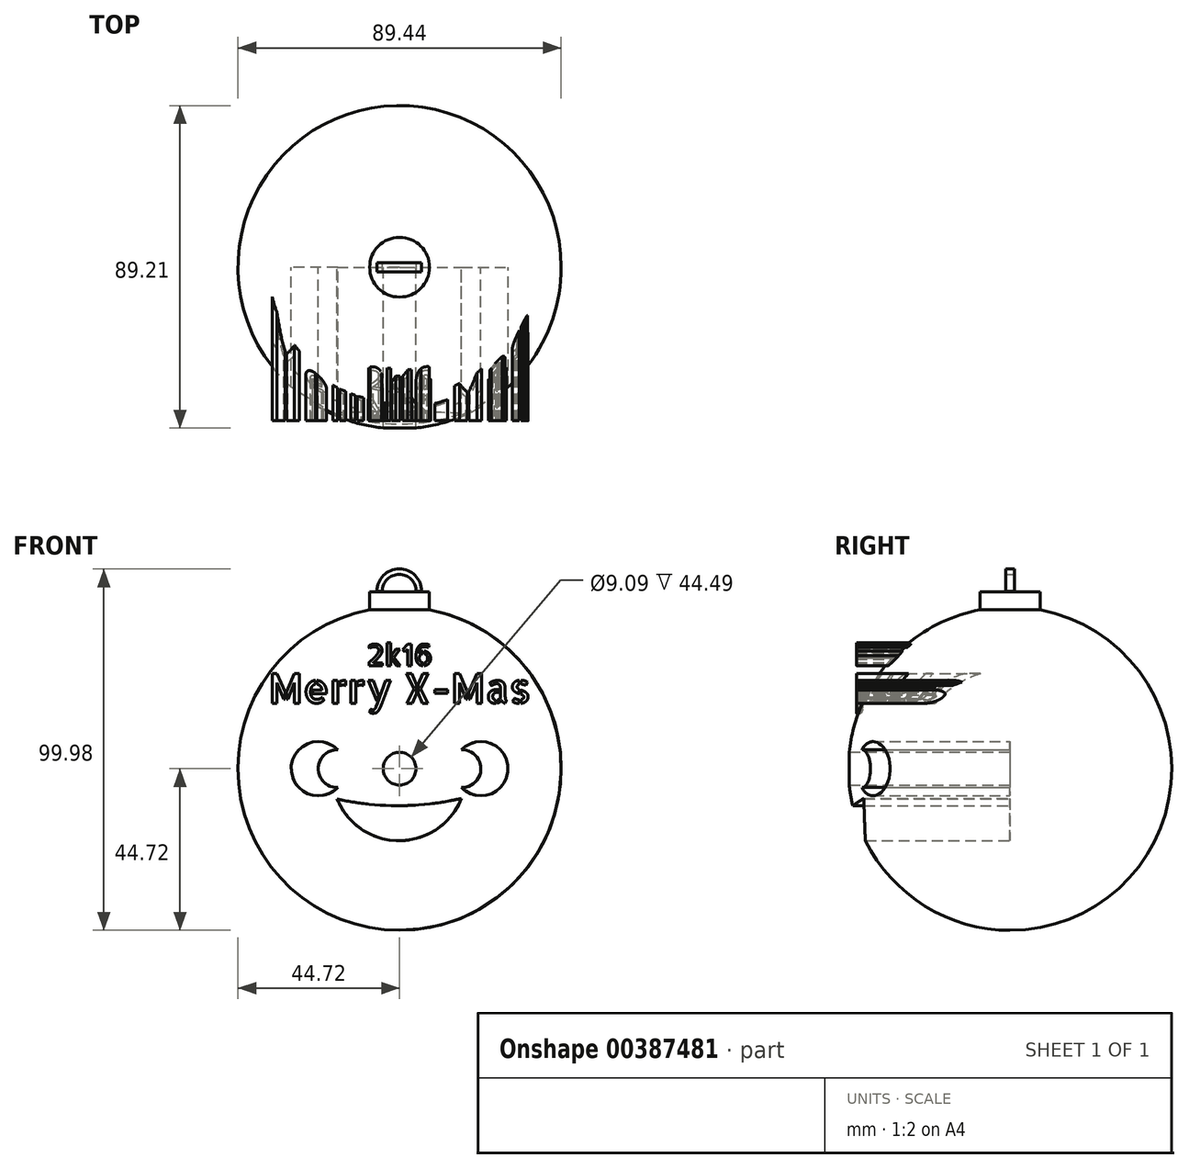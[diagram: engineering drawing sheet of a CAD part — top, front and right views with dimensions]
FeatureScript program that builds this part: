
annotation { "Feature Type Name" : "Feature", "Feature Type Description" : "" }
export const myFeature = defineFeature(function(context is Context, id is Id, definition is map)
    precondition{}
    {
        {
            var Q0;
            Q0=qCreatedBy(makeId("Front.planeOp"),FACE);
            var sketch = newSketch(context, id + "F0", { "sketchPlane" : qUnion([Q0])});
            skCircle(sketch, "E0", {"center": v(0, 0) * mm, "radius": 44.72 * mm});
            skLineSegment(sketch, "E1", {"start": v(0, 44.72) * mm, "end": v(0, -44.72) * mm});
            skSolve(sketch);
        }
        {
            var Q0;
            Q0=qCreatedBy(makeId("Front.planeOp"),FACE);
            var sketch = newSketch(context, id + "F1", { "sketchPlane" : qUnion([Q0])});
            skCircle(sketch, "E2", {"center": v(-22.5, 0) * mm, "radius": 7.5 * mm});
            skCircle(sketch, "E3", {"center": v(22.5, 0) * mm, "radius": 7.5 * mm});
            skArc(sketch, "E4", {"start": v(-17.12, 5.22) * mm, "mid": v(-22.5, 0) * mm, "end": v(-17.12, -5.22) * mm});
            skArc(sketch, "E5", {"start": v(17.12, -5.22) * mm, "mid": v(22.5, 0) * mm, "end": v(17.12, 5.22) * mm});
            skArc(sketch, "E6", {"start": v(-17.28, -8.4) * mm, "mid": v(-0.07, -10.25) * mm, "end": v(17.12, -8.21) * mm});
            skArc(sketch, "E7", {"start": v(-17.28, -8.4) * mm, "mid": v(-0.02, -19.93) * mm, "end": v(17.12, -8.21) * mm});
            skCircle(sketch, "E8", {"center": v(0, 0) * mm, "radius": 4.55 * mm});
            skSolve(sketch);
        }
        {
            var Q0;
            Q0=qCreatedBy(makeId("Front.planeOp"),FACE);
            var sketch = newSketch(context, id + "F2", { "sketchPlane" : qUnion([Q0])});
            skText(sketch, "E9", { "text": "Merry X-Mas", "fontName": "AllertaStencil-Regular.ttf"});
            skText(sketch, "E10", { "text": "2k16", "fontName": "AllertaStencil-Regular.ttf"});
            const initialGuessF2  = {"E9": [-0.03627, 0.01812, 1, 0, 0.00816], "E10": [-0.00913, 0.02852, 1, 0, 0.00594]};
            skSetInitialGuess(sketch, initialGuessF2);
            skSolve(sketch);
        }
        {
            var Q0;
            {var subQ0=sQuery(id+"F0.wireOp",EDGE,"E1");Q0=makeQuery(id+"F0.imprint","IMPRINT",FACE,{"disambiguationData":[TD([[makeQuery(id+"F0.imprint","IMPRINT",EDGE,{"derivedFrom":subQ0}),-1.0]])]});}
            var Q1;
            Q1=sQuery(id+"F0.wireOp",EDGE,"E1");
            revolve(context, id + "F3", {"entities" : qUnion([Q0]), "axis" : qUnion([Q1]), "revolveType" : RevolveType.FULL});
        }
        {
            var Q0;
            {var subQ0=sQuery(id+"F1.wireOp",EDGE,"E4");Q0=makeQuery(id+"F1.imprint","IMPRINT",FACE,{"disambiguationData":[TD([[makeQuery(id+"F1.imprint","IMPRINT",EDGE,{"derivedFrom":subQ0}),-1.0]])]});}
            var Q1;
            {var subQ0=sQuery(id+"F1.wireOp",EDGE,"E5");Q1=makeQuery(id+"F1.imprint","IMPRINT",FACE,{"disambiguationData":[TD([[makeQuery(id+"F1.imprint","IMPRINT",EDGE,{"derivedFrom":subQ0}),-1.0]])]});}
            var Q2;
            Q2=makeQuery(id+"F1.imprint","IMPRINT",FACE,{"disambiguationData":[TD([[makeQuery(id+"F1.imprint","IMPRINT",EDGE,{"derivedFrom":sQuery(id+"F1.wireOp",EDGE,"E6")}),-1.0]])]});
            var Q3;
            Q3=makeQuery(id+"F1.imprint","IMPRINT",FACE,{"disambiguationData":[TD([[makeQuery(id+"F1.imprint","IMPRINT",EDGE,{"derivedFrom":sQuery(id+"F1.wireOp",EDGE,"E8")}),1.0]])]});
            extrude(context, id + "F4", {"entities" : qUnion([Q0, Q1, Q2, Q3]), "operationType" : NewBodyOperationType.REMOVE, "depth" : 50 * mm});
        }
        {
            var Q0;
            Q0 = qSketchRegion(id + "F2", true);
            extrude(context, id + "F5", {"entities" : qUnion([Q0]), "operationType" : NewBodyOperationType.ADD, "depth" : 42.5 * mm});
        }
        {
            var Q0;
            Q0=qCreatedBy(makeId("Front.planeOp"),FACE);
            var sketch = newSketch(context, id + "F6", { "sketchPlane" : qUnion([Q0])});
            skLineSegment(sketch, "E11.bottom", {"start": v(8.27, 48.87) * mm, "end": v(-8.27, 48.87) * mm});
            skLineSegment(sketch, "E11.top", {"start": v(8.27, 40.6) * mm, "end": v(-8.27, 40.6) * mm});
            skLineSegment(sketch, "E11.left", {"start": v(8.27, 48.87) * mm, "end": v(8.27, 40.6) * mm});
            skLineSegment(sketch, "E11.right", {"start": v(-8.27, 48.87) * mm, "end": v(-8.27, 40.6) * mm});
            skPoint(sketch, "E11.middle", {"position": v(0, 44.73) * mm});
            skLineSegment(sketch, "E12", {"start": v(0, 48.87) * mm, "end": v(0, 40.6) * mm});
            skSolve(sketch);
        }
        {
            var Q0;
            {var subQ0=sQuery(id+"F6.wireOp",EDGE,"E11.right");Q0=makeQuery(id+"F6.imprint","IMPRINT",FACE,{"disambiguationData":[TD([[makeQuery(id+"F6.imprint","IMPRINT",EDGE,{"derivedFrom":subQ0}),1.0]])]});}
            var Q1;
            Q1=sQuery(id+"F6.wireOp",EDGE,"E12");
            revolve(context, id + "F7", {"operationType" : NewBodyOperationType.ADD, "entities" : qUnion([Q0]), "axis" : qUnion([Q1]), "revolveType" : RevolveType.FULL});
        }
        {
            var Q0;
            Q0=qCreatedBy(makeId("Front.planeOp"),FACE);
            var sketch = newSketch(context, id + "F8", { "sketchPlane" : qUnion([Q0])});
            skArc(sketch, "E13", {"start": v(-0.1, 53.75) * mm, "mid": v(-3.42, 52.38) * mm, "end": v(-4.8, 49.05) * mm});
            skPoint(sketch, "E13.startSnap0", {"position": v(-0.1, 49.05) * mm});
            skArc(sketch, "E14", {"start": v(-0.1, 53.75) * mm, "mid": v(3.23, 52.38) * mm, "end": v(4.6, 49.05) * mm});
            skArc(sketch, "E15", {"start": v(-0.1, 55.26) * mm, "mid": v(-4.48, 53.44) * mm, "end": v(-6.3, 49.05) * mm});
            skArc(sketch, "E16", {"start": v(-0.1, 55.26) * mm, "mid": v(4.3, 53.44) * mm, "end": v(6.1, 49.05) * mm});
            skLineSegment(sketch, "E17", {"start": v(-6.3, 49.05) * mm, "end": v(6.1, 49.05) * mm});
            skSolve(sketch);
        }
        {
            var Q0;
            {var subQ3=sQuery(id+"F8.wireOp",EDGE,"E13");Q0=makeQuery(id+"F8.imprint","IMPRINT",FACE,{"disambiguationData":[TD([[makeQuery(id+"F8.imprint","IMPRINT",EDGE,{"derivedFrom":subQ3}),-1.0]])]});}
            extrude(context, id + "F9", {"entities" : qUnion([Q0]), "endBound" : BoundingType.SYMMETRIC, "depth" : 2.5 * mm});
        }
    });
